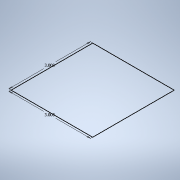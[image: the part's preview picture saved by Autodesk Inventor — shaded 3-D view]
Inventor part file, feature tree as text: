
AUTODESK INVENTOR PART (.ipt)
format: ipt  version: 2022 (Build 260153000, 153)  size: 120,320 bytes
history: native  units: in
note: dims shown in document units (in); Inventor stores cm internally (conversion verified against a paired STEP export)
features: sketch x2, extrude x1, projected_geometry x1
ambient origin geometry x8: Origin, YZ Plane, XZ Plane, XY Plane, X Axis, Y Axis, Z Axis, Center Point
bodies: Solid1 (feature_tree)
feature tree (4):
  extrude  "Extrusion1"  Depth=3.0in
  sketch  "Sketch2"  dims[d2=0.1in d3=0.0in d4=0.15in d5=0.7087in d6=0.7087in d7=1.1811in d9=1.0in d10=1.1811in d12=1.0in]
  sketch  "Sketch1"  dims[d0=3.0in d1=3.0in]
  projected_geometry  "Projected Loop1"
